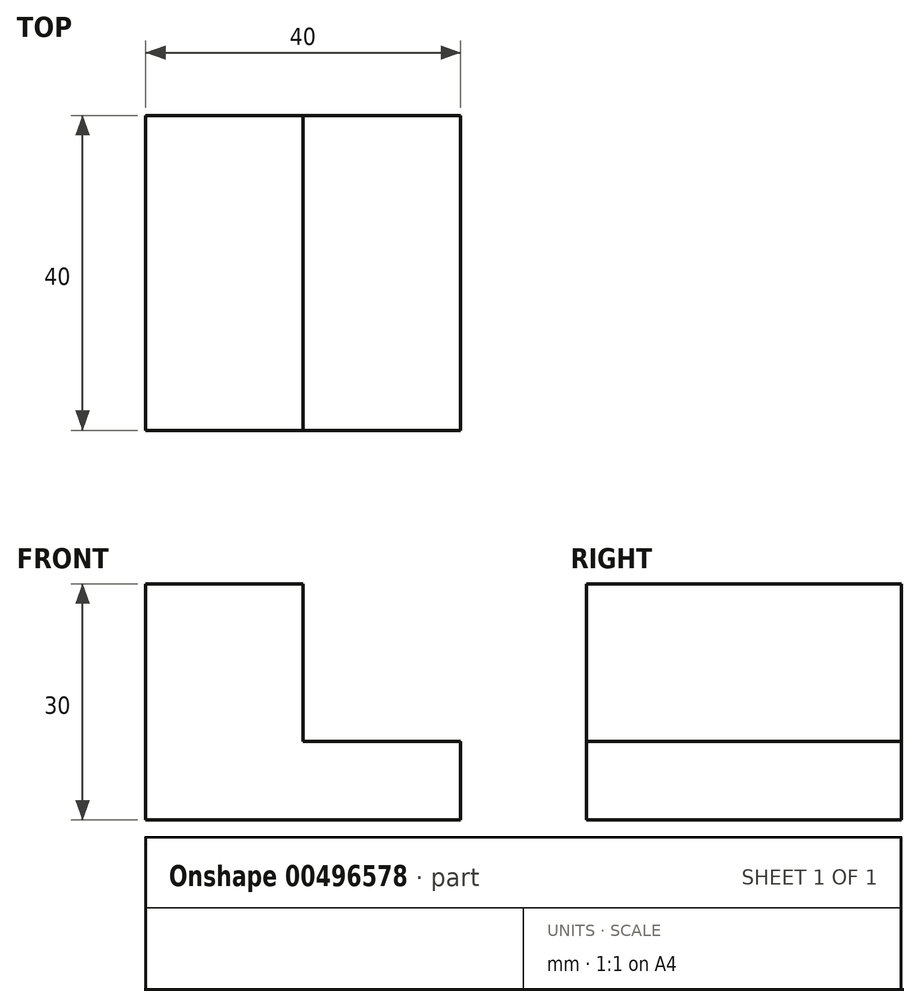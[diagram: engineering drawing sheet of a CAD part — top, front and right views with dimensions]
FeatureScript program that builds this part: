
annotation { "Feature Type Name" : "Feature", "Feature Type Description" : "" }
export const myFeature = defineFeature(function(context is Context, id is Id, definition is map)
    precondition{}
    {
        {
            var Q0;
            Q0=qCreatedBy(makeId("Front.planeOp"),FACE);
            var sketch = newSketch(context, id + "F0", { "sketchPlane" : qUnion([Q0])});
            skLineSegment(sketch, "E0", {"start": v(0, 0) * mm, "end": v(0, 30) * mm});
            skLineSegment(sketch, "E1", {"start": v(0, 0) * mm, "end": v(40, 0) * mm});
            skLineSegment(sketch, "E2", {"start": v(40, 0) * mm, "end": v(40, 10) * mm});
            skLineSegment(sketch, "E3", {"start": v(40, 10) * mm, "end": v(20, 10) * mm});
            skLineSegment(sketch, "E4", {"start": v(0, 30) * mm, "end": v(20, 30) * mm});
            skLineSegment(sketch, "E5", {"start": v(20, 10) * mm, "end": v(20, 30) * mm});
            skLineSegment(sketch, "E6", {"start": v(0, 0) * mm, "end": v(0, 40) * mm});
            skLineSegment(sketch, "E7", {"start": v(0, 40) * mm, "end": v(30, 40) * mm});
            skSolve(sketch);
        }
        {
            var Q0;
            Q0 = qSketchRegion(id + "F0", true);
            extrude(context, id + "F1", {"entities" : qUnion([Q0]), "depth" : 40 * mm});
        }
    });
